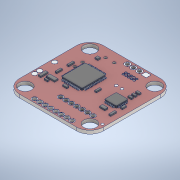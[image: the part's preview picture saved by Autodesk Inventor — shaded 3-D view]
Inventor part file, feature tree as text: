
AUTODESK INVENTOR PART (.ipt)
format: ipt  version: 2020 (Build 240168000, 168)  size: 684,544 bytes
history: mixed  units: mm
features: other x2, extrude x1, sketch x1, imported_body x1
ambient origin geometry x8: Origin, YZ Plane, XZ Plane, XY Plane, X Axis, Y Axis, Z Axis, Center Point
bodies: Body1 (imported_parasolid)
feature tree (5):
  other  "Твердое тело1"
  extrude  "Выдавливание1"  Depth=25.4mm TaperAngle=0.0deg
  sketch  "Эскиз1"
  other  "Cut-Extrude12"
  imported_body  NMx_Import_Brep_tag  [imported B-rep: ~676 faces, bbox_mm=[31.75, 3.937, 31.75]]
